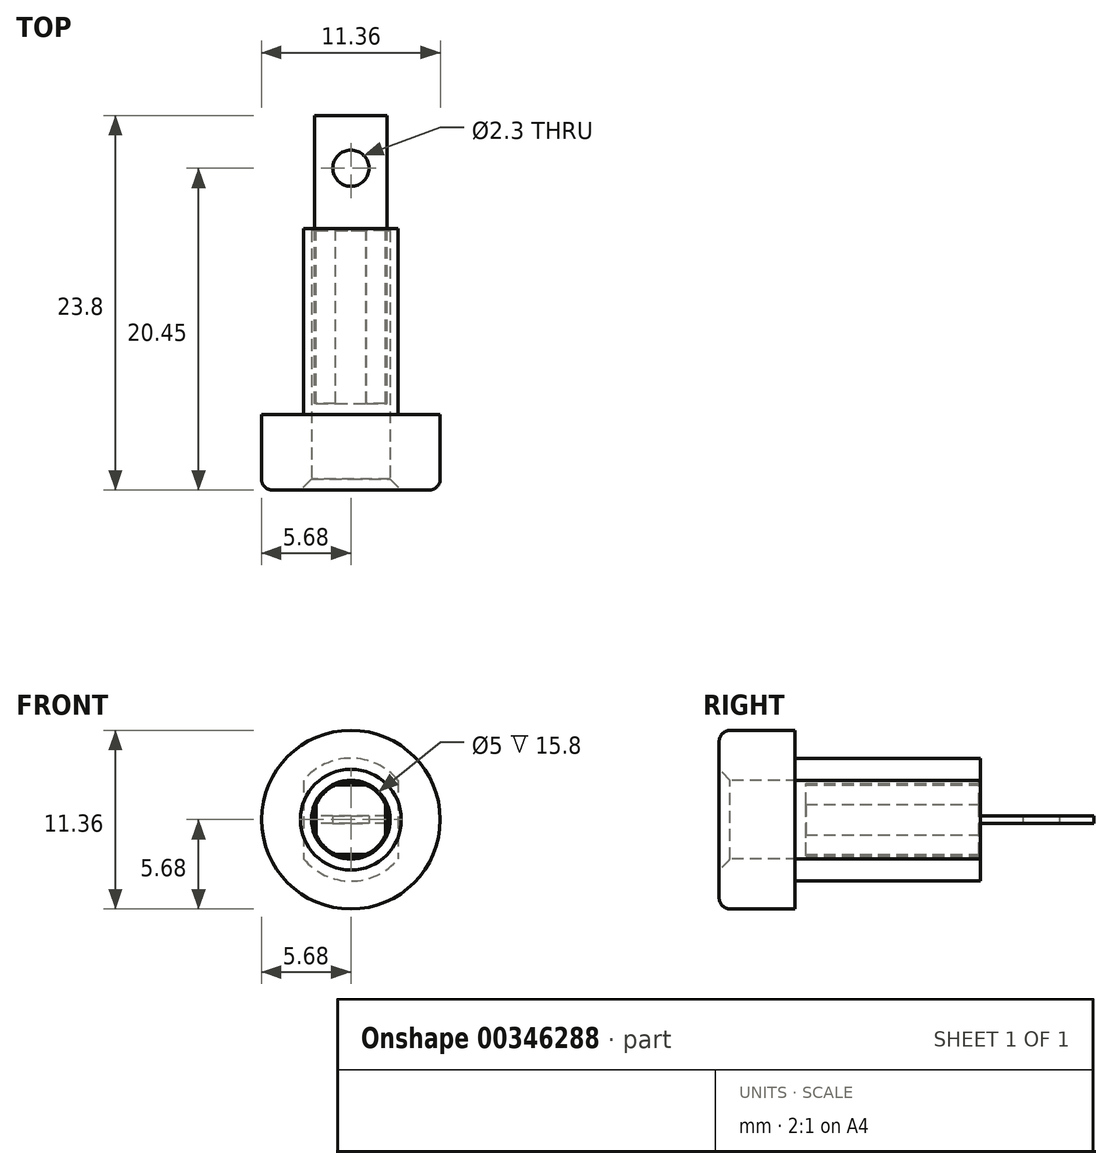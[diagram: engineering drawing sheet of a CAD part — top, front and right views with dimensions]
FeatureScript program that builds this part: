
annotation { "Feature Type Name" : "Feature", "Feature Type Description" : "" }
export const myFeature = defineFeature(function(context is Context, id is Id, definition is map)
    precondition{}
    {
        {
            var Q0;
            Q0=qCreatedBy(makeId("Front.planeOp"),FACE);
            var sketch = newSketch(context, id + "F0", { "sketchPlane" : qUnion([Q0])});
            skCircle(sketch, "E0", {"center": v(0, 0) * mm, "radius": 5.68 * mm});
            skCircle(sketch, "E1", {"center": v(0, 0) * mm, "radius": 2.5 * mm});
            skSolve(sketch);
        }
        {
            var Q0;
            Q0=makeQuery(id+"F0.imprint","IMPRINT",FACE,{"disambiguationData":[TD([[makeQuery(id+"F0.imprint","IMPRINT",EDGE,{"derivedFrom":sQuery(id+"F0.wireOp",EDGE,"E0")}),1.0]])]});
            extrude(context, id + "F1", {"entities" : qUnion([Q0]), "oppositeDirection" : true, "depth" : 4.8 * mm});
        }
        {
            var Q0;
            Q0=makeQuery(id+"F1.opExtrude","CAP_EDGE",EDGE,{"disambiguationData":[OSD([sQuery(id+"F0.wireOp",EDGE,"E0")])],"isStart":true});
            fillet(context, id + "F2", {"entities" : qUnion([Q0]), "radius" : 0.7 * mm, "tangentPropagation" : true, "allowEdgeOverflow" : false});
        }
        {
            var Q0;
            Q0=makeQuery(id+"F1.opExtrude","CAP_EDGE",EDGE,{"disambiguationData":[OSD([sQuery(id+"F0.wireOp",EDGE,"E1")])],"isStart":true});
            chamfer(context, id + "F3", {"entities" : qUnion([Q0]), "width" : 0.7 * mm, "tangentPropagation" : true});
        }
        {
            var Q0;
            Q0=makeQuery(id+"F1.opExtrude","CAP_FACE",FACE,{"disambiguationData":[OSD([sQuery(id+"F0.wireOp",EDGE,"E0"),sQuery(id+"F0.wireOp",EDGE,"E1")])],"isStart":false});
            var sketch = newSketch(context, id + "F4", { "sketchPlane" : qUnion([Q0])});
            skArc(sketch, "E2", {"start": v(-3, -2.5) * mm, "mid": v(0, -3.9) * mm, "end": v(3, -2.5) * mm});
            skLineSegment(sketch, "E3.left", {"start": v(3, 2.5) * mm, "end": v(3, -2.5) * mm});
            skLineSegment(sketch, "E3.right", {"start": v(-3, 2.5) * mm, "end": v(-3, -2.5) * mm});
            skArc(sketch, "E4.trimOffspring", {"start": v(3, 2.5) * mm, "mid": v(0, 3.9) * mm, "end": v(-3, 2.5) * mm});
            skSolve(sketch);
        }
        {
            var Q0;
            Q0=makeQuery(id+"F4.imprint","IMPRINT",FACE,{"disambiguationData":[TD([[makeQuery(id+"F4.imprint","IMPRINT",EDGE,{"derivedFrom":sQuery(id+"F4.wireOp",EDGE,"E2")}),1.0]])]});
            extrude(context, id + "F5", {"entities" : qUnion([Q0]), "operationType" : NewBodyOperationType.ADD, "depth" : 11.7 * mm});
        }
        {
            var Q0;
            Q0=makeQuery(id+"F5.opExtrude","CAP_FACE",FACE,{"disambiguationData":[OSD([sQuery(id+"F0.wireOp",EDGE,"E1"),sQuery(id+"F4.wireOp",EDGE,"E2"),sQuery(id+"F4.wireOp",EDGE,"E3.left"),sQuery(id+"F4.wireOp",EDGE,"E3.right"),sQuery(id+"F4.wireOp",EDGE,"E4.trimOffspring")])],"isStart":false});
            var sketch = newSketch(context, id + "F6", { "sketchPlane" : qUnion([Q0])});
            skPoint(sketch, "E5.middle", {"position": v(0, 0) * mm});
            skArc(sketch, "E6", {"start": v(-0.96, 2.2) * mm, "mid": v(-1.7, 1.7) * mm, "end": v(-2.2, 0.96) * mm});
            skArc(sketch, "E7", {"start": v(-0.98, 2.3) * mm, "mid": v(-2.5, 0) * mm, "end": v(-0.98, -2.3) * mm});
            skLineSegment(sketch, "E8.bottom", {"start": v(0.98, -2.3) * mm, "end": v(-0.98, -2.3) * mm});
            skLineSegment(sketch, "E8.top", {"start": v(0.98, 2.3) * mm, "end": v(-0.98, 2.3) * mm});
            skLineSegment(sketch, "E8.left", {"start": v(2.3, -0.98) * mm, "end": v(2.3, 0.98) * mm});
            skLineSegment(sketch, "E8.right", {"start": v(-2.3, -0.98) * mm, "end": v(-2.3, 0.69) * mm});
            skLineSegment(sketch, "E9.top", {"start": v(0.96, -2.2) * mm, "end": v(-0.96, -2.2) * mm});
            skLineSegment(sketch, "E9.left", {"start": v(2.2, 0.96) * mm, "end": v(2.2, -0.96) * mm});
            skLineSegment(sketch, "E9.right", {"start": v(-2.2, 0.96) * mm, "end": v(-2.2, -0.96) * mm});
            skLineSegment(sketch, "E10.trimOffspring", {"start": v(0.96, 2.2) * mm, "end": v(-0.96, 2.2) * mm});
            skPoint(sketch, "E11.orphan", {"position": v(2.3, 2.3) * mm});
            skPoint(sketch, "E12.orphan", {"position": v(2.2, 2.2) * mm});
            skPoint(sketch, "E13.orphan", {"position": v(-2.2, 2.2) * mm});
            skPoint(sketch, "E14.orphan", {"position": v(-2.3, 2.3) * mm});
            skPoint(sketch, "E15.orphan", {"position": v(-2.2, -2.2) * mm});
            skPoint(sketch, "E16.orphan", {"position": v(-2.3, -2.3) * mm});
            skPoint(sketch, "E17.orphan", {"position": v(2.3, -2.3) * mm});
            skPoint(sketch, "E18.orphan", {"position": v(2.2, -2.2) * mm});
            skArc(sketch, "E19.trimOffspring", {"start": v(2.2, 0.96) * mm, "mid": v(1.7, 1.7) * mm, "end": v(0.96, 2.2) * mm});
            skArc(sketch, "E20.trimOffspring", {"start": v(0.96, -2.2) * mm, "mid": v(1.7, -1.7) * mm, "end": v(2.2, -0.96) * mm});
            skArc(sketch, "E21.trimOffspring", {"start": v(0.98, -2.3) * mm, "mid": v(1.77, -1.77) * mm, "end": v(2.3, -0.98) * mm});
            skArc(sketch, "E22.trimOffspring", {"start": v(2.3, 0.98) * mm, "mid": v(1.77, 1.77) * mm, "end": v(0.98, 2.3) * mm});
            skLineSegment(sketch, "E23", {"start": v(-2.3, 0.69) * mm, "end": v(-2.3, 0.98) * mm});
            skArc(sketch, "E24.trimOffspring", {"start": v(-2.2, -0.96) * mm, "mid": v(-1.7, -1.7) * mm, "end": v(-0.96, -2.2) * mm});
            skSolve(sketch);
        }
        {
            var Q0;
            Q0=makeQuery(id+"F6.imprint","IMPRINT",FACE,{"disambiguationData":[TD([[makeQuery(id+"F6.imprint","IMPRINT",EDGE,{"derivedFrom":sQuery(id+"F6.wireOp",EDGE,"E6")}),-1.0]])]});
            extrude(context, id + "F7", {"entities" : qUnion([Q0]), "operationType" : NewBodyOperationType.ADD, "oppositeDirection" : true, "depth" : 11 * mm});
        }
        {
            var Q0;
            Q0=makeQuery(id+"F7.boolean.opBoolean","MERGE",FACE,{"derivedFrom":[makeQuery(id+"F5.opExtrude","CAP_FACE",FACE,{"disambiguationData":[OSD([sQuery(id+"F0.wireOp",EDGE,"E1"),sQuery(id+"F4.wireOp",EDGE,"E2"),sQuery(id+"F4.wireOp",EDGE,"E3.left"),sQuery(id+"F4.wireOp",EDGE,"E3.right"),sQuery(id+"F4.wireOp",EDGE,"E4.trimOffspring")])],"isStart":false}),makeQuery(id+"F7.opExtrude","CAP_FACE",FACE,{"disambiguationData":[OSD([sQuery(id+"F6.wireOp",EDGE,"E6"),sQuery(id+"F6.wireOp",EDGE,"E7"),sQuery(id+"F6.wireOp",EDGE,"E8.bottom"),sQuery(id+"F6.wireOp",EDGE,"E8.top"),sQuery(id+"F6.wireOp",EDGE,"E8.left"),sQuery(id+"F6.wireOp",EDGE,"E8.right"),sQuery(id+"F6.wireOp",EDGE,"E9.top"),sQuery(id+"F6.wireOp",EDGE,"E9.left"),sQuery(id+"F6.wireOp",EDGE,"E9.right"),sQuery(id+"F6.wireOp",EDGE,"E10.trimOffspring"),sQuery(id+"F6.wireOp",EDGE,"E19.trimOffspring"),sQuery(id+"F6.wireOp",EDGE,"E20.trimOffspring"),sQuery(id+"F6.wireOp",EDGE,"E21.trimOffspring"),sQuery(id+"F6.wireOp",EDGE,"E22.trimOffspring"),sQuery(id+"F6.wireOp",EDGE,"E23"),sQuery(id+"F6.wireOp",EDGE,"E24.trimOffspring")])],"isStart":true})]});
            var sketch = newSketch(context, id + "F8", { "sketchPlane" : qUnion([Q0])});
            skSolve(sketch);
        }
        {
            var Q0;
            {var subQ7=sQuery(id+"F4.wireOp",EDGE,"E2");Q0=makeQuery(id+"F8.imprint","IMPRINT",FACE,{"disambiguationData":[TD([[makeQuery(id+"F8.imprint","IMPRINT",EDGE,{"derivedFrom":makeQuery(id+"F5.opExtrude","CAP_EDGE",EDGE,{"disambiguationData":[OSD([subQ7])],"isStart":false})}),1.0]])]});}
            var Q1;
            {var subQ0=sQuery(id+"F6.wireOp",EDGE,"E23");var subQ1=sQuery(id+"F6.wireOp",EDGE,"E8.right");Q1=makeQuery(id+"F8.imprint","IMPRINT",FACE,{"disambiguationData":[TD([[makeQuery(id+"F8.imprint","IMPRINT",EDGE,{"derivedFrom":makeQuery(id+"F7.opExtrude","CAP_EDGE",EDGE,{"disambiguationData":[OSD([subQ1,subQ0])],"isStart":true})}),1.0]])]});}
            var Q2;
            {var subQ0=sQuery(id+"F6.wireOp",EDGE,"E8.bottom");Q2=makeQuery(id+"F8.imprint","IMPRINT",FACE,{"disambiguationData":[TD([[makeQuery(id+"F8.imprint","IMPRINT",EDGE,{"derivedFrom":makeQuery(id+"F7.opExtrude","CAP_EDGE",EDGE,{"disambiguationData":[OSD([subQ0])],"isStart":true})}),1.0]])]});}
            var Q3;
            Q3=makeQuery(id+"F8.imprint","IMPRINT",FACE,{"disambiguationData":[TD([[makeQuery(id+"F8.imprint","IMPRINT",EDGE,{"derivedFrom":makeQuery(id+"F7.opExtrude","CAP_EDGE",EDGE,{"disambiguationData":[OSD([sQuery(id+"F6.wireOp",EDGE,"E6")])],"isStart":true})}),1.0]])]});
            var Q4;
            {var subQ0=sQuery(id+"F6.wireOp",EDGE,"E8.left");Q4=makeQuery(id+"F8.imprint","IMPRINT",FACE,{"disambiguationData":[TD([[makeQuery(id+"F8.imprint","IMPRINT",EDGE,{"derivedFrom":makeQuery(id+"F7.opExtrude","CAP_EDGE",EDGE,{"disambiguationData":[OSD([subQ0])],"isStart":true})}),-1.0]])]});}
            var Q5;
            {var subQ0=sQuery(id+"F6.wireOp",EDGE,"E8.top");Q5=makeQuery(id+"F8.imprint","IMPRINT",FACE,{"disambiguationData":[TD([[makeQuery(id+"F8.imprint","IMPRINT",EDGE,{"derivedFrom":makeQuery(id+"F7.opExtrude","CAP_EDGE",EDGE,{"disambiguationData":[OSD([subQ0])],"isStart":true})}),-1.0]])]});}
            extrude(context, id + "F9", {"entities" : qUnion([Q0, Q1, Q2, Q3, Q4, Q5]), "operationType" : NewBodyOperationType.ADD, "depth" : 0.1 * mm});
        }
        {
            var Q0;
            Q0=makeQuery(id+"F9.opExtrude","CAP_FACE",FACE,{"disambiguationData":[OSD([sQuery(id+"F4.wireOp",EDGE,"E2"),sQuery(id+"F4.wireOp",EDGE,"E3.left"),sQuery(id+"F4.wireOp",EDGE,"E3.right"),sQuery(id+"F4.wireOp",EDGE,"E4.trimOffspring")])],"isStart":false});
            var sketch = newSketch(context, id + "F10", { "sketchPlane" : qUnion([Q0])});
            skPoint(sketch, "E25.middle", {"position": v(0, 0) * mm});
            skLineSegment(sketch, "E26", {"start": v(-2.3, 0.25) * mm, "end": v(-2.3, -0.25) * mm});
            skLineSegment(sketch, "E27", {"start": v(2.3, 0.25) * mm, "end": v(2.3, -0.25) * mm});
            skLineSegment(sketch, "E28.bottom", {"start": v(-2.3, 0.25) * mm, "end": v(2.3, 0.25) * mm});
            skLineSegment(sketch, "E28.top", {"start": v(-2.3, -0.25) * mm, "end": v(2.3, -0.25) * mm});
            skSolve(sketch);
        }
        {
            var Q0;
            Q0=makeQuery(id+"F10.imprint","IMPRINT",FACE,{"disambiguationData":[TD([[makeQuery(id+"F10.imprint","IMPRINT",EDGE,{"derivedFrom":sQuery(id+"F10.wireOp",EDGE,"E26")}),1.0]])]});
            extrude(context, id + "F11", {"entities" : qUnion([Q0]), "operationType" : NewBodyOperationType.ADD, "depth" : 7.2 * mm});
        }
        {
            var Q0;
            Q0=makeQuery(id+"F11.opExtrude","SWEPT_FACE",FACE,{"disambiguationData":[OSD([sQuery(id+"F10.wireOp",EDGE,"E28.top")])]});
            var sketch = newSketch(context, id + "F12", { "sketchPlane" : qUnion([Q0])});
            skCircle(sketch, "E29", {"center": v(0, -20.45) * mm, "radius": 1.15 * mm});
            skPoint(sketch, "E29.centerSnap0", {"position": v(0, -23.8) * mm});
            skSolve(sketch);
        }
        {
            var Q0;
            Q0=makeQuery(id+"F12.imprint","IMPRINT",FACE,{"disambiguationData":[TD([[makeQuery(id+"F12.imprint","IMPRINT",EDGE,{"derivedFrom":sQuery(id+"F12.wireOp",EDGE,"E29")}),1.0]])]});
            extrude(context, id + "F13", {"entities" : qUnion([Q0]), "operationType" : NewBodyOperationType.REMOVE, "oppositeDirection" : true, "depth" : 0.5 * mm});
        }
    });
